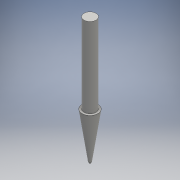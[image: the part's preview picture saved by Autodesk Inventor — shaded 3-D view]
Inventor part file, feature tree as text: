
AUTODESK INVENTOR PART (.ipt)
format: ipt  version: 2016 (Build 200138000, 138)  size: 102,400 bytes
history: native  units: mm
features: revolve x1, sketch x1
ambient origin geometry x8: Origin, YZ Plane, XZ Plane, XY Plane, X Axis, Y Axis, Z Axis, Center Point
bodies: Solid1 (feature_tree)
feature tree (2):
  revolve  "Revolution1"  [1 undecoded]
  sketch  "Sketch1"  dims[d7=0.25mm d9=0.001mm d11=90.0deg]
note: 1 required parameter value undecoded (feature->parameter linkage not recoverable at this tier; creation-order binding heuristic only, values carry confidence <= 0.55)
